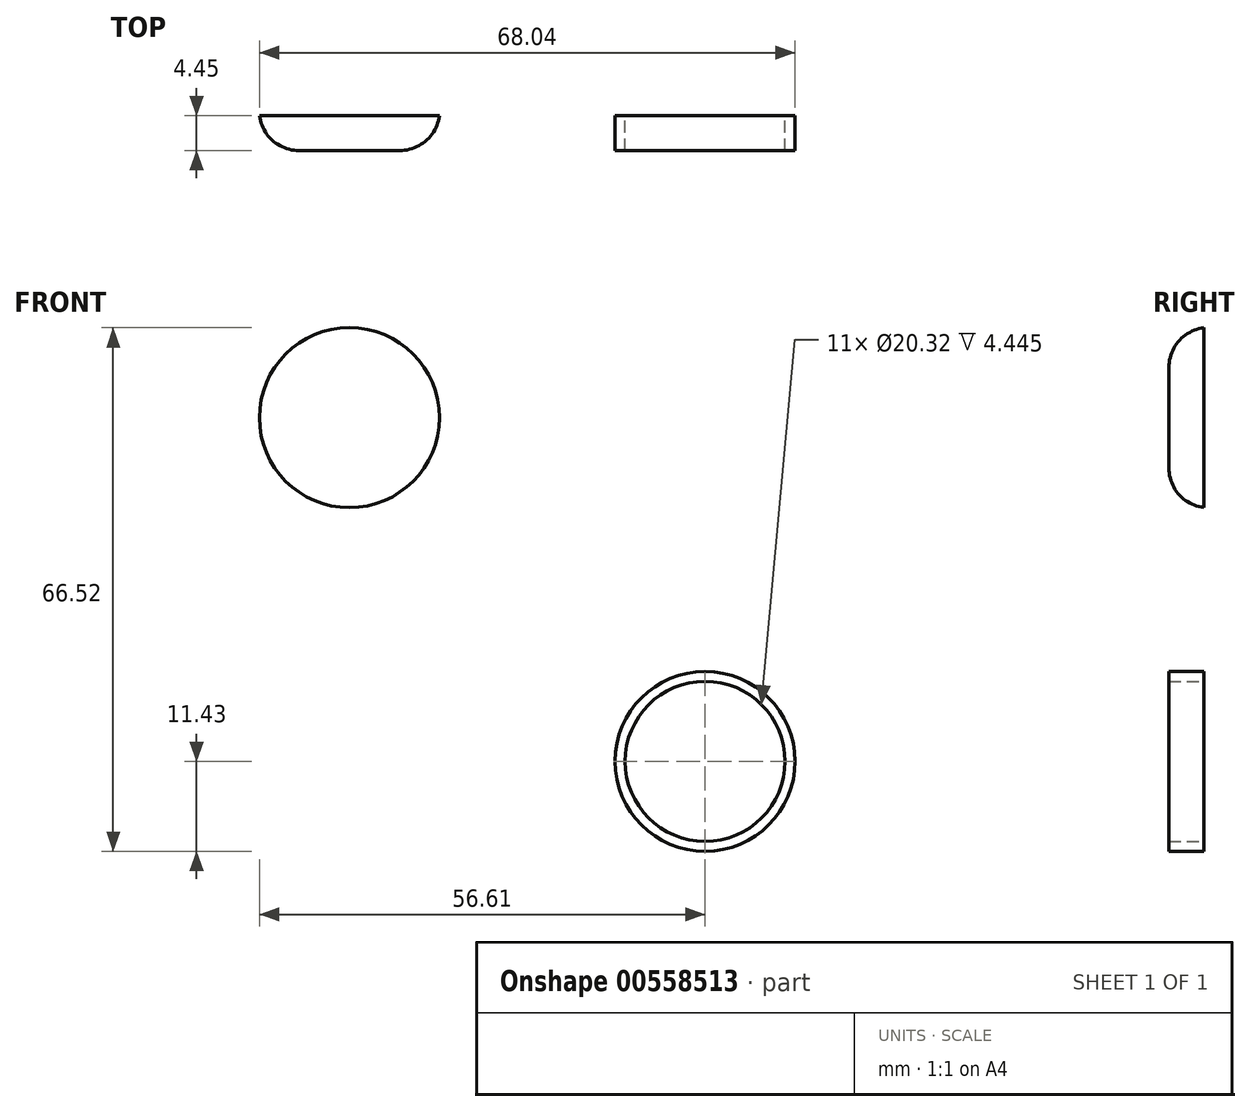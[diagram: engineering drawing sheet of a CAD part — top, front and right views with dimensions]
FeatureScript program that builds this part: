
annotation { "Feature Type Name" : "Feature", "Feature Type Description" : "" }
export const myFeature = defineFeature(function(context is Context, id is Id, definition is map)
    precondition{}
    {
        {
            var Q0;
            Q0=qCreatedBy(makeId("Front.planeOp"),FACE);
            var sketch = newSketch(context, id + "F0", { "sketchPlane" : qUnion([Q0])});
            skCircle(sketch, "E0", {"center": v(0, 0) * mm, "radius": 11.43 * mm});
            skCircle(sketch, "E1", {"center": v(0, 0) * mm, "radius": 10.16 * mm});
            skSolve(sketch);
        }
        {
            var Q0;
            Q0 = qSketchRegion(id + "F0", true);
            var Q1;
            Q1=makeQuery(id+"F0.imprint","IMPRINT",FACE,{"disambiguationData":[TD([[makeQuery(id+"F0.imprint","IMPRINT",EDGE,{"derivedFrom":sQuery(id+"F0.wireOp",EDGE,"E0")}),1.0]])]});
            extrude(context, id + "F1", {"entities" : qUnion([Q0, Q1]), "depth" : 4.44 * mm, "offsetDistance" : 25.4 * mm});
        }
        {
            var Q0;
            Q0=qCreatedBy(makeId("Front.planeOp"),FACE);
            var sketch = newSketch(context, id + "F2", { "sketchPlane" : qUnion([Q0])});
            skCircle(sketch, "E2", {"center": v(-45.18, 43.66) * mm, "radius": 11.43 * mm});
            skSolve(sketch);
        }
        {
            var Q0;
            Q0 = qSketchRegion(id + "F2", true);
            extrude(context, id + "F3", {"entities" : qUnion([Q0]), "depth" : 4.44 * mm, "offsetDistance" : 25.4 * mm});
        }
        {
            var Q0;
            Q0=makeQuery(id+"F3.opExtrude","CAP_FACE",FACE,{"disambiguationData":[OSD([sQuery(id+"F2.wireOp",EDGE,"E2")])],"isStart":false});
            fillet(context, id + "F4", {"entities" : qUnion([Q0]), "radius" : 5.08 * mm, "tangentPropagation" : true, "allowEdgeOverflow" : false});
        }
    });
